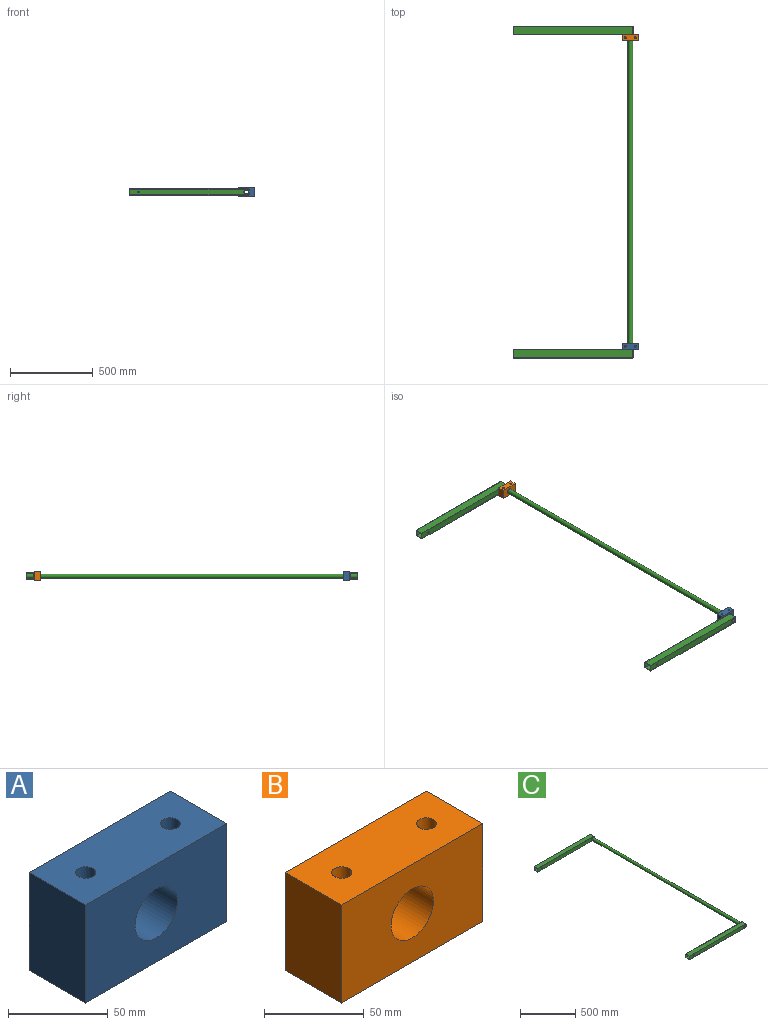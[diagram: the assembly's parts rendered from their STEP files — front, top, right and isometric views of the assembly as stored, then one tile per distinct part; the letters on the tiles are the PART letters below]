
ASSEMBLY  parts=3 mates=3
PART A: 9 faces, bbox 100x40x60 mm
  f0: plane 100x40mm, normal (0,0,-1), area 3842.9mm2, adj f1,f3,f5,f6,f7,f8
  f1: plane 60x40mm, normal (-1,0,0), area 2400mm2, adj f0,f2,f5,f6
  f2: plane 100x40mm, normal (0,0,1), area 3842.9mm2, adj f1,f3,f5,f6,f7,f8
  f3: plane 60x40mm, normal (1,0,0), area 2400mm2, adj f0,f2,f5,f6
  f4: cylinder r=15mm len=40mm, axis (0,1,0), area 3769.9mm2, adj f5,f6
  f5: plane 100x60mm, normal (0,-1,0), area 5293.1mm2, adj f0,f1,f2,f3,f4
  f6: plane 100x60mm, normal (0,1,0), area 5293.1mm2, adj f0,f1,f2,f3,f4
  f7: cylinder r=5mm len=60mm, axis (0,0,1), area 1885mm2, adj f0,f2
  f8: cylinder r=5mm len=60mm, axis (0,0,1), area 1885mm2, adj f0,f2
PART B: 9 faces, bbox 100x40x60 mm
  f0: plane 100x40mm, normal (0,0,-1), area 3842.9mm2, adj f1,f3,f5,f6,f7,f8
  f1: plane 60x40mm, normal (-1,0,0), area 2400mm2, adj f0,f2,f5,f6
  f2: plane 100x40mm, normal (0,0,1), area 3842.9mm2, adj f1,f3,f5,f6,f7,f8
  f3: plane 60x40mm, normal (1,0,0), area 2400mm2, adj f0,f2,f5,f6
  f4: cylinder r=15mm len=40mm, axis (0,-1,0), area 3769.9mm2, adj f5,f6
  f5: plane 100x60mm, normal (0,1,0), area 5293.1mm2, adj f0,f1,f2,f3,f4
  f6: plane 100x60mm, normal (0,-1,0), area 5293.1mm2, adj f0,f1,f2,f3,f4
  f7: cylinder r=5mm len=60mm, axis (0,0,1), area 1885mm2, adj f0,f2
  f8: cylinder r=5mm len=60mm, axis (0,0,1), area 1885mm2, adj f0,f2
PART C: 34 faces, bbox 724.8x2000x40 mm
  f0: plane 719.84x50mm, normal (0,0,-1), area 35992mm2, adj f3,f4,f17,f33
  f1: plane 722.84x44mm, normal (0,0,-1), area 31805mm2, adj f5,f6,f18,f33
  f2: plane 722.84x44mm, normal (0,0,1), area 31805mm2, adj f5,f6,f17,f33
  f3: plane 724.84x40mm, normal (0,-1,0), area 28403.1mm2, adj f0,f14,f15,f17,f18,f20,f29,f33
  f4: plane 724.84x40mm, normal (0,1,0), area 28148.6mm2, adj f0,f14,f16,f17,f18,f19,f30,f33
  f5: plane 724.84x34mm, normal (0,1,0), area 23820.6mm2, adj f1,f2,f15,f17,f18,f20,f31,f33
  f6: plane 724.84x34mm, normal (0,-1,0), area 23820.6mm2, adj f1,f2,f16,f17,f18,f19,f31,f33
  f7: plane 724.84x34mm, normal (0,-1,0), area 23820.6mm2, adj f10,f11,f21,f23,f24,f25,f26,f32
  f8: plane 724.84x34mm, normal (0,1,0), area 23820.6mm2, adj f10,f11,f21,f22,f24,f25,f27,f32
  f9: plane 724.84x40mm, normal (0,-1,0), area 28148.6mm2, adj f12,f22,f24,f25,f27,f28,f30,f32
  f10: plane 722.84x44mm, normal (0,0,1), area 31805mm2, adj f7,f8,f25,f32
  f11: plane 722.84x44mm, normal (0,0,-1), area 31805mm2, adj f7,f8,f24,f32
  f12: plane 719.84x50mm, normal (0,0,-1), area 35992mm2, adj f9,f13,f25,f32
  f13: plane 724.84x40mm, normal (0,1,0), area 28403.1mm2, adj f12,f23,f24,f25,f26,f28,f29,f32
  f14: plane 719.84x50mm, normal (0,0,1), area 35992mm2, adj f3,f4,f18,f33
  f15: plane 30x3mm, normal (1,0,0), area 90mm2, adj f3,f5,f17,f18
  f16: plane 30x3mm, normal (1,0,0), area 90mm2, adj f4,f6,f17,f18
  f17: plane 50x5mm, normal (0.71,0,-0.71), area 229.1mm2, adj f0,f2,f3,f4,f5,f6,f15,f16
  f18: plane 50x5mm, normal (0.71,0,0.71), area 229.1mm2, adj f1,f3,f4,f5,f6,f14,f15,f16
  f19: cylinder r=6mm len=12mm, axis (0,1,0), area 113.1mm2, adj f4,f6
  f20: cylinder r=6mm len=12mm, axis (0,1,0), area 113.1mm2, adj f3,f5
  f21: cylinder r=15mm len=44mm, axis (0,-1,0), area 4146.9mm2, adj f7,f8
  f22: cylinder r=6mm len=12mm, axis (0,1,0), area 113.1mm2, adj f8,f9
  f23: cylinder r=6mm len=12mm, axis (0,1,0), area 113.1mm2, adj f7,f13
  f24: plane 50x5mm, normal (0.71,0,0.71), area 229.1mm2, adj f7,f8,f9,f11,f13,f26,f27,f28
  f25: plane 50x5mm, normal (0.71,0,-0.71), area 229.1mm2, adj f7,f8,f9,f10,f12,f13,f26,f27
  f26: plane 30x3mm, normal (1,0,0), area 90mm2, adj f7,f13,f24,f25
  f27: plane 30x3mm, normal (1,0,0), area 90mm2, adj f8,f9,f24,f25
  f28: plane 719.84x50mm, normal (0,0,1), area 35992mm2, adj f9,f13,f24,f32
  f29: cylinder r=12mm len=2000mm, axis (0,-1,0), area 150796.4mm2, adj f3,f13
  f30: cylinder r=15mm len=1900mm, axis (0,-1,0), area 179070.8mm2, adj f4,f9
  f31: cylinder r=15mm len=44mm, axis (0,-1,0), area 4146.9mm2, adj f5,f6
  f32: plane 50x40mm, normal (-1,0,0), area 504mm2, adj f7,f8,f9,f10,f11,f12,f13,f28
  f33: plane 50x40mm, normal (-1,0,0), area 504mm2, adj f0,f1,f2,f3,f4,f5,f6,f14
PLACE A t=(80.18,-1860.67,-36)mm
PLACE B t=(80.18,1859.33,-36)mm
PLACE C t=(80.18,-0.67,-36)mm
MATE revolute A.f4 <-> C.f21  axis (0,1,0) through (730.18,24.33,-36)mm
MATE revolute B.f4 <-> C.f21  axis (0,1,0) through (730.18,1924.33,-36)mm
MATE planar A.f2 <-> B.f2  axis (0,0,1) through (730.18,44.33,-6)mm
